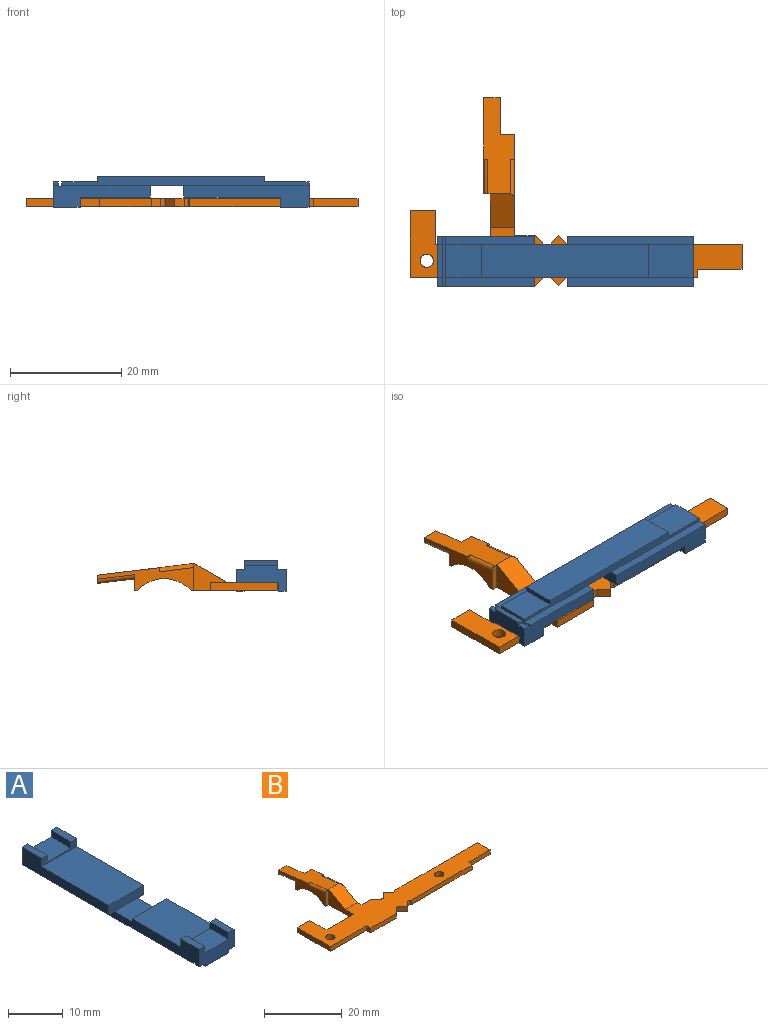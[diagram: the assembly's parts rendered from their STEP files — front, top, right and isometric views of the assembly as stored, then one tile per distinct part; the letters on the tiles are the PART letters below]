
ASSEMBLY  parts=2 mates=1
PART A: 42 faces, bbox 9x45.9x5.4 mm
  f0: plane 6x0.9mm, normal (0,0,-1), area 5.4mm2, adj f11,f13,f17,f40
  f1: plane 44.4x1.5mm, normal (-1,0,0), area 53.6mm2, adj f3,f9,f10,f12,f14,f15,f16,f18
  f2: plane 44.4x1.5mm, normal (1,0,0), area 53.6mm2, adj f5,f9,f10,f12,f14,f15,f16,f18
  f3: plane 15.9x1.5mm, normal (0,0,-1), area 23.9mm2, adj f1,f4,f27,f39
  f4: plane 17.4x3.9mm, normal (-1,0,0), area 45mm2, adj f3,f8,f17,f25,f27,f30,f36,f39
  f5: plane 15.9x1.5mm, normal (0,0,-1), area 23.8mm2, adj f2,f26,f27,f39
  f6: plane 6.15x4.8mm, normal (0,0,1), area 29.5mm2, adj f17,f30,f35,f37
  f7: plane 6.15x5.1mm, normal (0,0,1), area 31.4mm2, adj f16,f29,f31,f33
  f8: plane 12.6x9mm, normal (0,0,1), area 113.4mm2, adj f4,f26,f27,f30
  f9: plane 6x6mm, normal (0,0,1), area 36mm2, adj f1,f2,f22,f27
  f10: plane 6x0.9mm, normal (0,1,0), area 5.4mm2, adj f1,f2,f14,f18
  f11: plane 0.9x0.6mm, normal (-1,0,0), area 0.5mm2, adj f0,f17,f25,f40
  f12: plane 6x0.9mm, normal (0,-1,0), area 5.4mm2, adj f1,f2,f14,f15
  f13: plane 0.9x0.6mm, normal (1,0,0), area 0.5mm2, adj f0,f17,f28,f40
  f14: plane 30x6mm, normal (0,0,-1), area 180mm2, adj f1,f2,f10,f12
  f15: plane 6.45x6mm, normal (0,0,-1), area 38.7mm2, adj f1,f2,f12,f39
  f16: plane 9x4.5mm, normal (0,1,0), area 29.5mm2, adj f1,f2,f7,f18,f19,f20,f21,f24
  f17: plane 9x4.5mm, normal (0,-1,0), area 29.5mm2, adj f0,f4,f6,f11,f13,f25,f26,f28
  f18: plane 7.95x6mm, normal (0,0,-1), area 47.7mm2, adj f1,f2,f10,f16
  f19: plane 22.5x1.5mm, normal (0,0,-1), area 33.7mm2, adj f1,f16,f21,f22
  f20: plane 22.5x3.9mm, normal (1,0,0), area 56.4mm2, adj f16,f22,f23,f24,f29,f34
  f21: plane 22.5x3.9mm, normal (-1,0,0), area 56.4mm2, adj f16,f19,f22,f23,f29,f32
  f22: plane 9x2.1mm, normal (0,-1,0), area 18.9mm2, adj f9,f19,f20,f21,f23,f24
  f23: plane 17.4x9mm, normal (0,0,1), area 156.6mm2, adj f20,f21,f22,f29
  f24: plane 22.5x1.5mm, normal (0,0,-1), area 33.7mm2, adj f2,f16,f20,f22
  f25: plane 1.5x0.9mm, normal (0,0,-1), area 1.4mm2, adj f4,f11,f17,f40
  f26: plane 17.4x3.9mm, normal (1,0,0), area 45mm2, adj f5,f8,f17,f27,f28,f30,f38,f39
  f27: plane 9x2.1mm, normal (0,1,0), area 18.9mm2, adj f3,f4,f5,f8,f9,f26
  f28: plane 1.5x0.9mm, normal (0,0,-1), area 1.4mm2, adj f13,f17,f26,f40
  f29: plane 9x1.8mm, normal (0,-1,0), area 7mm2, adj f7,f20,f21,f23,f31,f32,f33,f34
  f30: plane 9x1.8mm, normal (0,1,0), area 7mm2, adj f4,f6,f8,f26,f35,f36,f37,f38
  f31: plane 5.1x1.5mm, normal (1,0,0), area 7.7mm2, adj f7,f16,f29,f32
  f32: plane 5.1x1.43mm, normal (0,0,1), area 7.3mm2, adj f16,f21,f29,f31
  f33: plane 5.1x1.5mm, normal (-1,0,0), area 7.7mm2, adj f7,f16,f29,f34
  f34: plane 5.1x1.43mm, normal (0,0,1), area 7.3mm2, adj f16,f20,f29,f33
  f35: plane 4.8x1.5mm, normal (1,0,0), area 7.2mm2, adj f6,f17,f30,f36
  f36: plane 4.8x1.43mm, normal (0,0,1), area 6.8mm2, adj f4,f17,f30,f35
  f37: plane 4.8x1.5mm, normal (-1,0,0), area 7.2mm2, adj f6,f17,f30,f38
  f38: plane 4.8x1.43mm, normal (0,0,1), area 6.8mm2, adj f17,f26,f30,f37
  f39: plane 9x0.9mm, normal (0,-1,0), area 6.3mm2, adj f1,f2,f3,f4,f5,f15,f26,f41
  f40: plane 9x0.9mm, normal (0,1,0), area 6.3mm2, adj f0,f4,f11,f13,f25,f26,f28,f41
  f41: plane 9x0.6mm, normal (0,0,-1), area 5.4mm2, adj f4,f26,f39,f40
PART B: 46 faces, bbox 59.6x33.9x5.1 mm
  f0: plane 4.93x1.2mm, normal (0,-1,0), area 5.8mm2, adj f1,f2,f32,f35,f42
  f1: plane 17.27x5.55mm, normal (0,0.12,0.99), area 70.3mm2, adj f0,f25,f33,f35,f36,f37,f39,f42
  f2: plane 9x4.93mm, normal (-1,0,0), area 23.6mm2, adj f0,f26,f31,f32,f33
  f3: plane 12x1.47mm, normal (-1,0,0), area 17.6mm2, adj f4,f29,f31,f32
  f4: plane 13.2x1.47mm, normal (0,-1,0), area 19.4mm2, adj f3,f5,f31,f32
  f5: plane 1.5x1.47mm, normal (-1,0,0), area 2.2mm2, adj f4,f6,f31,f32
  f6: plane 9.3x1.47mm, normal (0,-1,0), area 13.7mm2, adj f5,f7,f31,f32
  f7: plane 1.68x1.68mm, normal (0.71,-0.71,0), area 3.5mm2, adj f6,f8,f31,f32
  f8: cylinder r=0.6mm len=1.47mm, axis (0,0,-1), area 1.4mm2, adj f7,f9,f31,f32
  f9: plane 1.68x1.68mm, normal (-0.71,-0.71,0), area 3.5mm2, adj f8,f10,f31,f32
  f10: plane 1.68x1.68mm, normal (0.71,-0.71,0), area 3.5mm2, adj f9,f11,f31,f32
  f11: cylinder r=0.6mm len=1.47mm, axis (0,0,-1), area 1.4mm2, adj f10,f12,f31,f32
  f12: plane 1.47x0.18mm, normal (-0.71,-0.71,0), area 0.4mm2, adj f11,f13,f31,f32
  f13: plane 22.2x1.47mm, normal (0,-1,0), area 32.6mm2, adj f12,f14,f31,f32
  f14: plane 1.5x1.47mm, normal (1,0,0), area 2.2mm2, adj f13,f15,f31,f32
  f15: plane 8x1.47mm, normal (0,-1,0), area 11.8mm2, adj f14,f16,f31,f32
  f16: plane 4.5x1.47mm, normal (1,0,0), area 6.6mm2, adj f15,f17,f31,f32
  f17: plane 30.2x1.47mm, normal (0,1,0), area 44.4mm2, adj f16,f18,f31,f32
  f18: plane 1.47x0.18mm, normal (-0.71,0.71,0), area 0.4mm2, adj f17,f19,f31,f32
  f19: cylinder r=0.6mm len=1.47mm, axis (0,0,-1), area 1.4mm2, adj f18,f20,f31,f32
  f20: plane 1.68x1.68mm, normal (0.71,0.71,0), area 3.5mm2, adj f19,f21,f31,f32
  f21: plane 1.68x1.68mm, normal (-0.71,0.71,0), area 3.5mm2, adj f20,f22,f31,f32
  f22: cylinder r=0.6mm len=1.47mm, axis (0,0,-1), area 1.4mm2, adj f21,f23,f31,f32
  f23: plane 1.68x1.68mm, normal (0.71,0.71,0), area 3.5mm2, adj f22,f24,f31,f32
  f24: plane 3.75x1.47mm, normal (0,1,0), area 5.5mm2, adj f23,f25,f31,f32
  f25: plane 18.22x4.31mm, normal (1,0,0), area 47.5mm2, adj f1,f24,f31,f32,f33,f39,f40,f41
  f26: plane 9.9x1.47mm, normal (0,1,0), area 14.6mm2, adj f2,f27,f31,f32
  f27: plane 6x1.47mm, normal (1,0,0), area 8.8mm2, adj f26,f29,f31,f32
  f28: cylinder r=1.2mm len=2.4mm, axis (0,0,-1), area 11.1mm2, adj f31,f32
  f29: plane 4.5x1.47mm, normal (0,1,0), area 6.6mm2, adj f3,f27,f31,f32
  f30: cylinder r=1.2mm len=2.4mm, axis (0,0,-1), area 11.1mm2, adj f31,f32
  f31: plane 59.6x13.5mm, normal (0,0,1), area 401.8mm2, adj f2,f3,f4,f5,f6,f7,f8,f9
  f32: plane 59.6x17mm, normal (0,0,-1), area 430.7mm2, adj f0,f2,f3,f4,f5,f6,f7,f8
  f33: plane 6x4.35mm, normal (0,-0.5,0.87), area 29.9mm2, adj f1,f2,f25,f31,f45
  f34: plane 6.55x2.25mm, normal (0,-0.12,-0.99), area 14.9mm2, adj f36,f37,f38,f39
  f35: plane 17.27x4.18mm, normal (-1,0,0), area 31.1mm2, adj f0,f1,f32,f36,f38,f39,f40,f41
  f36: plane 3x1.47mm, normal (0,1,0), area 4.3mm2, adj f1,f34,f35,f37,f38
  f37: plane 6.55x2.27mm, normal (1,0,0), area 9.6mm2, adj f1,f34,f36,f39
  f38: cylinder r=0.75mm len=6.73mm, axis (0,0.99,-0.12), area 7.8mm2, adj f34,f35,f36,f39
  f39: plane 5.55x3.62mm, normal (0,1,0), area 15.8mm2, adj f1,f25,f34,f35,f37,f38,f41
  f40: cylinder r=6.5mm len=9.72mm, axis (1,0,0), area 60.9mm2, adj f25,f32,f35,f41
  f41: plane 5.55x0.5mm, normal (0,0,-1), area 2.8mm2, adj f25,f35,f39,f40
  f42: cylinder r=0.75mm len=6.34mm, axis (0,0.99,-0.12), area 7.4mm2, adj f0,f1,f35,f43
  f43: plane 0.75x0.74mm, normal (0,-0.99,0.12), area 0.1mm2, adj f1,f35,f42
  f44: plane 0.75x0.74mm, normal (0,-0.99,0.12), area 0.1mm2, adj f1,f25,f45
  f45: cylinder r=0.75mm len=7.33mm, axis (0,0.99,-0.12), area 7.8mm2, adj f1,f25,f33,f44
PLACE A rot(axis=(-0.71,-0.71,0),180deg) t=(27.45,-0.73,4.81)mm
PLACE B t=(-0.41,-0.65,0.18)mm
MATE slider A.f17 <-> B.f27  axis (-1,0,0) through (4.5,2.35,0.91)mm
